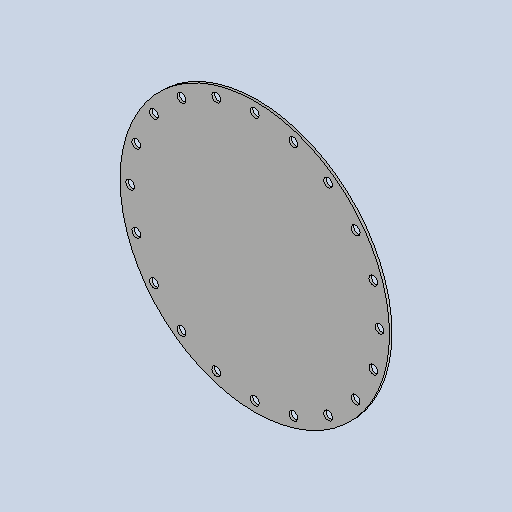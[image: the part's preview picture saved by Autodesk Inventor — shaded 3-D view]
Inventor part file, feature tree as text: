
AUTODESK INVENTOR PART (.ipt)
format: ipt  version: 2025.1 (Build 291241020, 241B)  size: 209,408 bytes
history: native  units: mm
features: sketch x2, other x2, extrude x1, pattern_circular x1
ambient origin geometry x8: Origin, YZ Plane, XZ Plane, XY Plane, X Axis, Y Axis, Z Axis, Center Point
bodies: Solid1 (feature_tree)
feature tree (6):
  extrude  "Extrusion1"  Depth=6.0mm TaperAngle=0.0deg
  pattern_circular  "Circular Pattern1"  Count=62  [1 undecoded]
  sketch  "Sketch1"  dims[d0=670.0mm d1=6.0mm d2=0.0mm]
  sketch  "Sketch2"  dims[d3=22.0mm d4=620.0mm d5=8.0mm d6=8.0mm d7=0.0mm d8=200.0mm d9=360.0deg]
  other  "Cut1"
  other  "Definition1"
note: 1 required parameter value undecoded (feature->parameter linkage not recoverable at this tier; creation-order binding heuristic only, values carry confidence <= 0.55)
